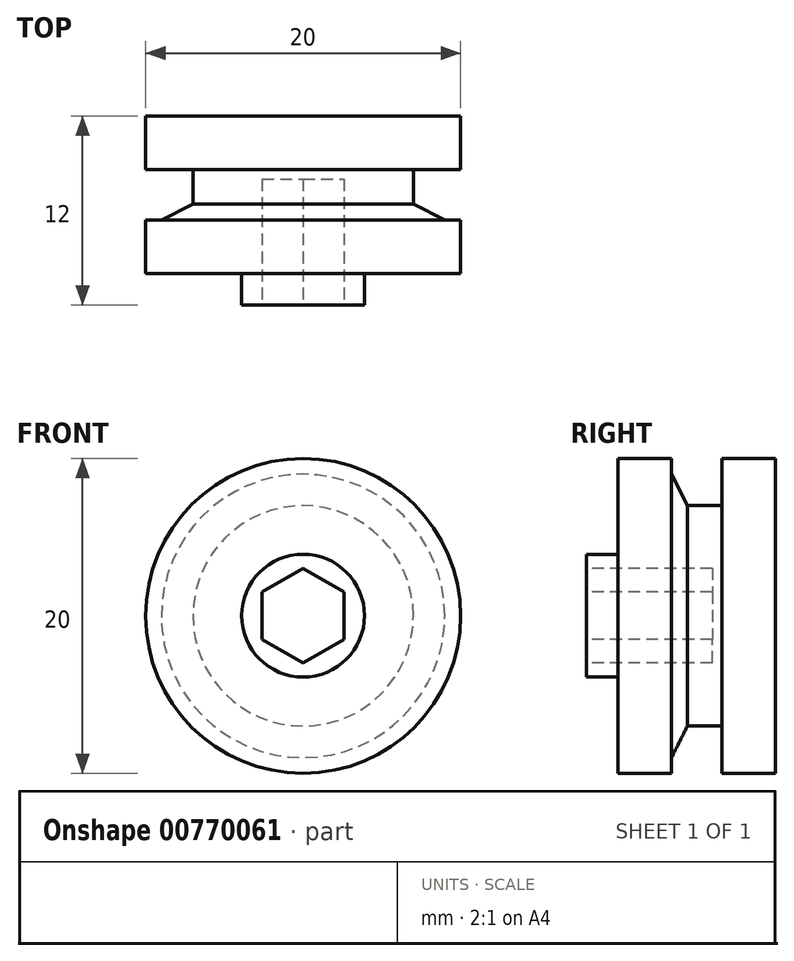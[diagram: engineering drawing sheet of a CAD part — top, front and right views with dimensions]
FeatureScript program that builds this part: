
annotation { "Feature Type Name" : "Feature", "Feature Type Description" : "" }
export const myFeature = defineFeature(function(context is Context, id is Id, definition is map)
    precondition{}
    {
        {
            var Q0;
            Q0=qCreatedBy(makeId("Right.planeOp"),FACE);
            var sketch = newSketch(context, id + "F0", { "sketchPlane" : qUnion([Q0])});
            skLineSegment(sketch, "E0", {"start": v(0, -30.02) * mm, "end": v(0, 9.98) * mm, "construction": true});
            skLineSegment(sketch, "E1", {"start": v(0, 6.98) * mm, "end": v(-1.6, 6.98) * mm});
            skLineSegment(sketch, "E2", {"start": v(-1.6, 6.98) * mm, "end": v(-1.6, 9.98) * mm});
            skLineSegment(sketch, "E3", {"start": v(-1.6, 9.98) * mm, "end": v(-5, 9.98) * mm});
            skLineSegment(sketch, "E4", {"start": v(-5, 9.98) * mm, "end": v(-5, -0.02) * mm});
            skLineSegment(sketch, "E5.MirrorCS", {"start": v(5, 9.98) * mm, "end": v(5, -0.02) * mm});
            skLineSegment(sketch, "E6.MirrorCS", {"start": v(1.6, 9.98) * mm, "end": v(5, 9.98) * mm});
            skLineSegment(sketch, "E7.MirrorCS", {"start": v(1.6, 6.98) * mm, "end": v(1.6, 9.98) * mm});
            skLineSegment(sketch, "E8.MirrorCS", {"start": v(0, 6.98) * mm, "end": v(1.6, 6.98) * mm});
            skLineSegment(sketch, "E9", {"start": v(-5, -0.02) * mm, "end": v(5, -0.02) * mm});
            skSolve(sketch);
        }
        {
            var Q0;
            Q0=makeQuery(id+"F0.imprint","IMPRINT",FACE,{"disambiguationData":[TD([[makeQuery(id+"F0.imprint","IMPRINT",EDGE,{"derivedFrom":sQuery(id+"F0.wireOp",EDGE,"E1")}),1.0]])]});
            var Q1;
            Q1=sQuery(id+"F0.wireOp",EDGE,"E9");
            revolve(context, id + "F1", {"surfaceOperationType" : NewSurfaceOperationType.NEW, "entities" : qUnion([Q0]), "axis" : qUnion([Q1]), "revolveType" : RevolveType.FULL});
        }
        {
            var Q0;
            Q0=makeQuery(id+"F1.opRevolve","SWEPT_FACE",FACE,{"disambiguationData":[OSD([sQuery(id+"F0.wireOp",EDGE,"E4")])]});
            var sketch = newSketch(context, id + "F2", { "sketchPlane" : qUnion([Q0])});
            skCircle(sketch, "E10.cCircle", {"center": v(0, 0) * mm, "radius": 2.6 * mm, "construction": true});
            skLineSegment(sketch, "E10.0", {"start": v(2.6, 1.5) * mm, "end": v(2.6, -1.5) * mm});
            skLineSegment(sketch, "E10.1", {"start": v(2.6, -1.5) * mm, "end": v(0, -3) * mm});
            skLineSegment(sketch, "E10.2", {"start": v(0, -3) * mm, "end": v(-2.6, -1.5) * mm});
            skLineSegment(sketch, "E10.3", {"start": v(-2.6, -1.5) * mm, "end": v(-2.6, 1.5) * mm});
            skLineSegment(sketch, "E10.4", {"start": v(-2.6, 1.5) * mm, "end": v(0, 3) * mm});
            skLineSegment(sketch, "E10.5", {"start": v(0, 3) * mm, "end": v(2.6, 1.5) * mm});
            skPoint(sketch, "E10.0.midPoint", {"position": v(2.6, 0) * mm});
            skCircle(sketch, "E11", {"center": v(0, 0) * mm, "radius": 3.9 * mm});
            skSolve(sketch);
        }
        {
            var Q0;
            Q0=makeQuery(id+"F2.imprint","IMPRINT",FACE,{"disambiguationData":[TD([[makeQuery(id+"F2.imprint","IMPRINT",EDGE,{"derivedFrom":sQuery(id+"F2.wireOp",EDGE,"E10.0")}),-1.0]])]});
            extrude(context, id + "F3", {"entities" : qUnion([Q0]), "operationType" : NewBodyOperationType.REMOVE, "oppositeDirection" : true, "depth" : 6 * mm, "offsetDistance" : 25 * mm});
        }
        {
            var Q0;
            Q0=makeQuery(id+"F1.opRevolve","SWEPT_EDGE",EDGE,{"disambiguationData":[OSD([sQuery(id+"F0.wireOp",EDGE,"E1"),sQuery(id+"F0.wireOp",EDGE,"E2")])]});
            chamfer(context, id + "F4", {"entities" : qUnion([Q0]), "chamferType" : ChamferType.TWO_OFFSETS, "width1" : 2 * mm, "oppositeDirection" : false, "width2" : 1 * mm, "tangentPropagation" : true});
        }
        {
            var Q0;
            Q0 = qSketchRegion(id + "F2", true);
            extrude(context, id + "F5", {"entities" : qUnion([Q0]), "operationType" : NewBodyOperationType.ADD, "depth" : 2 * mm, "offsetDistance" : 25 * mm});
        }
    });
